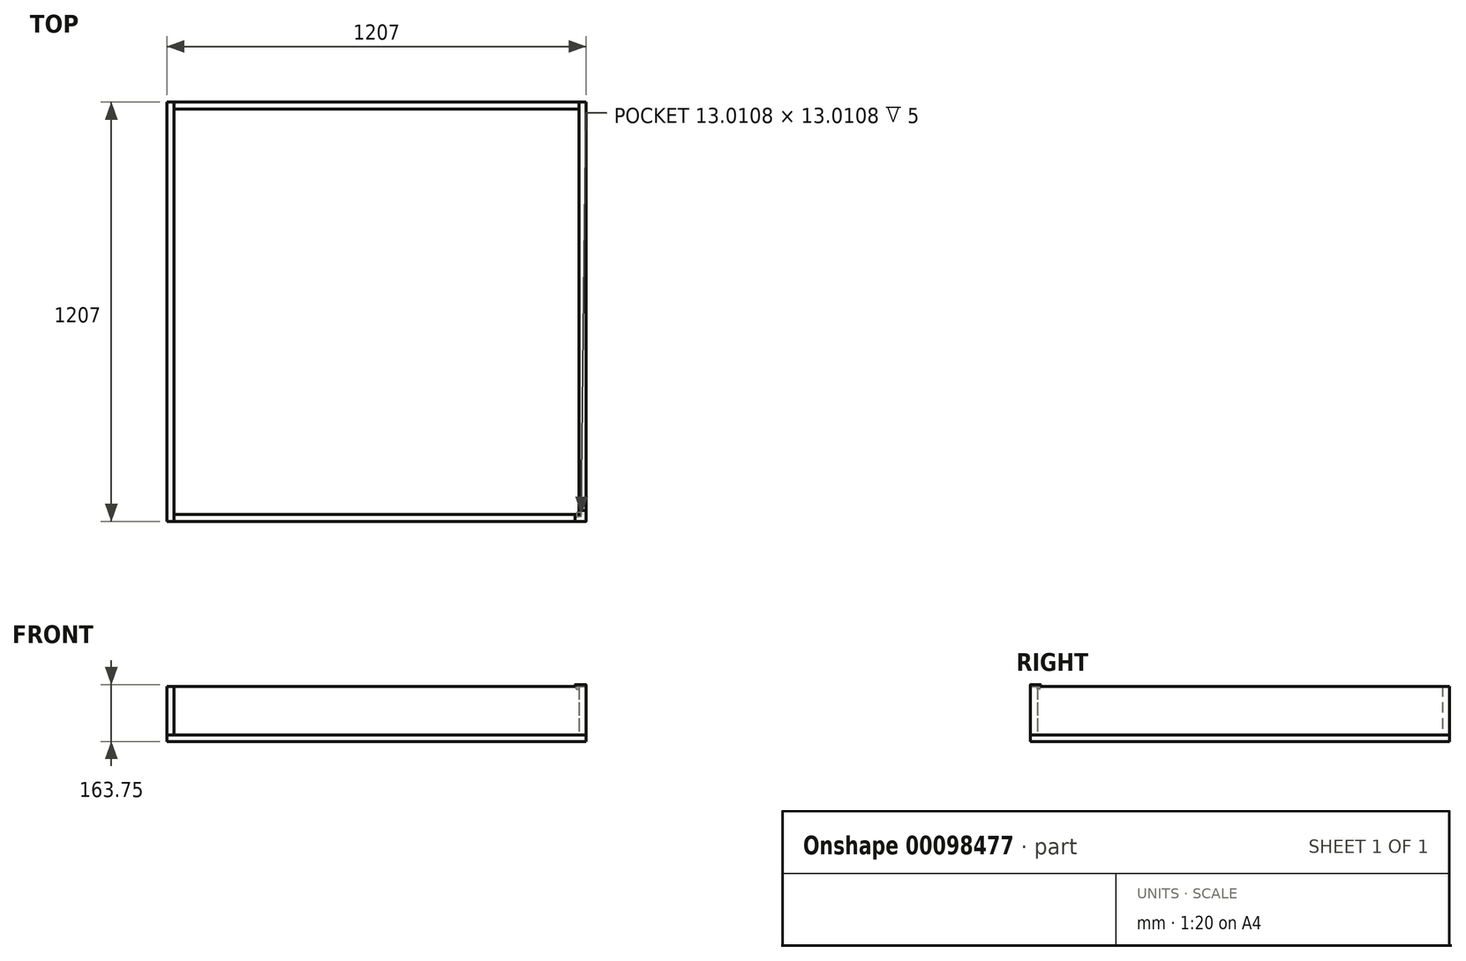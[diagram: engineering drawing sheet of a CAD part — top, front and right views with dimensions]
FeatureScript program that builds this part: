
annotation { "Feature Type Name" : "Feature", "Feature Type Description" : "" }
export const myFeature = defineFeature(function(context is Context, id is Id, definition is map)
    precondition{}
    {
        {
            var Q0;
            Q0=qCreatedBy(makeId("Top.planeOp"),FACE);
            var sketch = newSketch(context, id + "F0", { "sketchPlane" : qUnion([Q0])});
            skLineSegment(sketch, "E0.bottom", {"start": v(603.5, -603.5) * mm, "end": v(-603.5, -603.5) * mm});
            skLineSegment(sketch, "E0.top", {"start": v(603.5, 603.5) * mm, "end": v(-603.5, 603.5) * mm});
            skLineSegment(sketch, "E0.left", {"start": v(603.5, -603.5) * mm, "end": v(603.5, 603.5) * mm});
            skLineSegment(sketch, "E0.right", {"start": v(-603.5, -603.5) * mm, "end": v(-603.5, 603.5) * mm});
            skPoint(sketch, "E0.middle", {"position": v(0, 0) * mm});
            skSolve(sketch);
        }
        {
            var Q0;
            Q0 = qSketchRegion(id + "F0", true);
            extrude(context, id + "F1", {"entities" : qUnion([Q0]), "depth" : 19.05 * mm});
        }
        {
            var Q0;
            Q0=makeQuery(id+"F1.opExtrude","CAP_FACE",FACE,{"disambiguationData":[OSD([sQuery(id+"F0.wireOp",EDGE,"E0.bottom"),sQuery(id+"F0.wireOp",EDGE,"E0.top"),sQuery(id+"F0.wireOp",EDGE,"E0.left"),sQuery(id+"F0.wireOp",EDGE,"E0.right")])],"isStart":false});
            var sketch = newSketch(context, id + "F2", { "sketchPlane" : qUnion([Q0])});
            skLineSegment(sketch, "E1.0", {"start": v(-603.5, -603.5) * mm, "end": v(-603.5, 603.5) * mm});
            skLineSegment(sketch, "E1.1", {"start": v(603.5, 603.5) * mm, "end": v(-603.5, 603.5) * mm});
            skLineSegment(sketch, "E1.2", {"start": v(603.5, -603.5) * mm, "end": v(-603.5, -603.5) * mm});
            skLineSegment(sketch, "E2", {"start": v(-583.3, 603.5) * mm, "end": v(-583.3, -603.5) * mm});
            skSolve(sketch);
        }
        {
            var Q0;
            {var subQ0=sQuery(id+"F2.wireOp",EDGE,"E1.0");Q0=makeQuery(id+"F2.imprint","IMPRINT",FACE,{"disambiguationData":[TD([[makeQuery(id+"F2.imprint","IMPRINT",EDGE,{"derivedFrom":subQ0}),-1.0]])]});}
            extrude(context, id + "F3", {"entities" : qUnion([Q0]), "depth" : 139.7 * mm});
        }
        {
            var Q0;
            Q0=makeQuery(id+"F3.opExtrude","SWEPT_BODY",BODY,{"disambiguationData":[OSD([sQuery(id+"F2.wireOp",EDGE,"E1.0"),sQuery(id+"F2.wireOp",EDGE,"E1.1"),sQuery(id+"F2.wireOp",EDGE,"E1.2"),sQuery(id+"F2.wireOp",EDGE,"E2")])]});
            var Q1;
            Q1=qCreatedBy(makeId("Right.planeOp"),FACE);
            mirror(context, id + "F4", {"entities" : qUnion([Q0]), "mirrorPlane" : qUnion([Q1])});
        }
        {
            var Q0;
            Q0=makeQuery(id+"F1.opExtrude","CAP_FACE",FACE,{"disambiguationData":[OSD([sQuery(id+"F0.wireOp",EDGE,"E0.bottom"),sQuery(id+"F0.wireOp",EDGE,"E0.top"),sQuery(id+"F0.wireOp",EDGE,"E0.left"),sQuery(id+"F0.wireOp",EDGE,"E0.right")])],"isStart":false});
            var sketch = newSketch(context, id + "F5", { "sketchPlane" : qUnion([Q0])});
            skLineSegment(sketch, "E3.0", {"start": v(583.3, 603.5) * mm, "end": v(-583.3, 603.5) * mm});
            skLineSegment(sketch, "E3.1", {"start": v(-583.3, 603.5) * mm, "end": v(-583.3, -603.5) * mm});
            skLineSegment(sketch, "E3.2", {"start": v(583.3, 603.5) * mm, "end": v(583.3, -603.5) * mm});
            skLineSegment(sketch, "E4", {"start": v(-583.3, 583.3) * mm, "end": v(583.3, 583.3) * mm});
            skPoint(sketch, "E5.orphan", {"position": v(-603.5, 603.5) * mm});
            skPoint(sketch, "E6.orphan", {"position": v(603.5, 603.5) * mm});
            skSolve(sketch);
        }
        {
            var Q0;
            {var subQ0=sQuery(id+"F5.wireOp",EDGE,"E3.0");Q0=makeQuery(id+"F5.imprint","IMPRINT",FACE,{"disambiguationData":[TD([[makeQuery(id+"F5.imprint","IMPRINT",EDGE,{"derivedFrom":subQ0}),1.0]])]});}
            extrude(context, id + "F6", {"entities" : qUnion([Q0]), "depth" : 139.7 * mm});
        }
        {
            var Q0;
            Q0=makeQuery(id+"F6.opExtrude","SWEPT_BODY",BODY,{"disambiguationData":[OSD([sQuery(id+"F5.wireOp",EDGE,"E3.0"),sQuery(id+"F5.wireOp",EDGE,"E3.1"),sQuery(id+"F5.wireOp",EDGE,"E3.2"),sQuery(id+"F5.wireOp",EDGE,"E4")])]});
            var Q1;
            Q1=qCreatedBy(makeId("Front.planeOp"),FACE);
            mirror(context, id + "F7", {"entities" : qUnion([Q0]), "mirrorPlane" : qUnion([Q1])});
        }
        {
            var Q0;
            Q0=makeQuery(id+"F4.opPattern","COPY",FACE,{"derivedFrom":makeQuery(id+"F3.opExtrude","CAP_FACE",FACE,{"disambiguationData":[OSD([sQuery(id+"F2.wireOp",EDGE,"E1.0"),sQuery(id+"F2.wireOp",EDGE,"E1.1"),sQuery(id+"F2.wireOp",EDGE,"E1.2"),sQuery(id+"F2.wireOp",EDGE,"E2")])],"isStart":false}),"instanceName":"1"});
            cPlane(context, id + "F8", {"entities" : qUnion([Q0]), "cplaneType" : CPlaneType.OFFSET, "offset" : 0 * mm, "width" : 150 * mm, "height" : 150 * mm});
        }
        {
            var Q0;
            Q0=qCreatedBy(id+"F8.planeOp",FACE);
            var sketch = newSketch(context, id + "F9", { "sketchPlane" : qUnion([Q0])});
            skLineSegment(sketch, "E7.0", {"start": v(583.3, 603.5) * mm, "end": v(583.3, -603.5) * mm});
            skLineSegment(sketch, "E7.1", {"start": v(-583.3, -583.3) * mm, "end": v(583.3, -583.3) * mm});
            skLineSegment(sketch, "E7.2", {"start": v(583.3, -603.5) * mm, "end": v(603.5, -603.5) * mm});
            skLineSegment(sketch, "E7.3", {"start": v(603.5, -603.5) * mm, "end": v(603.5, 603.5) * mm});
            skLineSegment(sketch, "E7.4", {"start": v(583.3, -603.5) * mm, "end": v(-583.3, -603.5) * mm});
            skLineSegment(sketch, "E8", {"start": v(603.5, -603.5) * mm, "end": v(583.3, -583.3) * mm, "construction": true});
            skLineSegment(sketch, "E9", {"start": v(583.3, -583.3) * mm, "end": v(583.3, -583.3) * mm});
            skLineSegment(sketch, "E10", {"start": v(583.3, -583.3) * mm, "end": v(578.2, -588.4) * mm, "construction": true});
            skLineSegment(sketch, "E11.MirrorCS", {"start": v(583.3, -583.3) * mm, "end": v(588.4, -578.2) * mm, "construction": true});
            skLineSegment(sketch, "E12", {"start": v(588.4, -578.2) * mm, "end": v(586.98, -576.8) * mm});
            skLineSegment(sketch, "E13", {"start": v(586.98, -576.8) * mm, "end": v(576.8, -586.98) * mm});
            skLineSegment(sketch, "E14", {"start": v(578.2, -588.4) * mm, "end": v(576.8, -586.98) * mm});
            skLineSegment(sketch, "E15.MirrorCS", {"start": v(588.4, -578.2) * mm, "end": v(589.8, -579.62) * mm});
            skLineSegment(sketch, "E16.MirrorCS", {"start": v(589.8, -579.62) * mm, "end": v(579.62, -589.8) * mm});
            skLineSegment(sketch, "E17.MirrorCS", {"start": v(578.2, -588.4) * mm, "end": v(579.62, -589.8) * mm});
            skLineSegment(sketch, "E18.1", {"start": v(571.14, -586.98) * mm, "end": v(579.62, -595.46) * mm});
            skLineSegment(sketch, "E18.3", {"start": v(593.8, -581.28) * mm, "end": v(579.62, -595.46) * mm});
            skLineSegment(sketch, "E18.4", {"start": v(585.4, -572.71) * mm, "end": v(571.14, -586.98) * mm});
            skLineSegment(sketch, "E19.trimOffspring", {"start": v(585.4, -572.71) * mm, "end": v(593.8, -581.28) * mm});
            skSolve(sketch);
        }
        {
            var Q0;
            {var subQ1=sQuery(id+"F9.wireOp",EDGE,"E12");Q0=makeQuery(id+"F9.imprint","IMPRINT",FACE,{"disambiguationData":[TD([[makeQuery(id+"F9.imprint","IMPRINT",EDGE,{"derivedFrom":subQ1}),-1.0]])]});}
            var Q1;
            {var subQ0=sQuery(id+"F9.wireOp",EDGE,"E18.4");var subQ1=sQuery(id+"F9.wireOp",EDGE,"E7.0");var subQ2=makeQuery(id+"F9.imprint","INTERSECT",VERTEX,{"derivedFrom":[subQ1,subQ0]});Q1=makeQuery(id+"F9.imprint","IMPRINT",FACE,{"disambiguationData":[TD([[makeQuery(id+"F9.imprint","IMPRINT",EDGE,{"disambiguationData":[TD([[subQ2,-1.0]])],"derivedFrom":subQ1}),-1.0]])]});}
            var Q2;
            {var subQ0=sQuery(id+"F9.wireOp",EDGE,"E14");Q2=makeQuery(id+"F9.imprint","IMPRINT",FACE,{"disambiguationData":[TD([[makeQuery(id+"F9.imprint","IMPRINT",EDGE,{"derivedFrom":subQ0}),1.0]])]});}
            extrude(context, id + "F10", {"entities" : qUnion([Q0, Q1, Q2]), "depth" : 5 * mm});
        }
        {
            var Q0;
            Q0=makeQuery(id+"F10.opExtrude","CAP_FACE",FACE,{"disambiguationData":[OSD([sQuery(id+"F9.wireOp",EDGE,"E12"),sQuery(id+"F9.wireOp",EDGE,"E13"),sQuery(id+"F9.wireOp",EDGE,"E14"),sQuery(id+"F9.wireOp",EDGE,"E15.MirrorCS"),sQuery(id+"F9.wireOp",EDGE,"E16.MirrorCS"),sQuery(id+"F9.wireOp",EDGE,"E17.MirrorCS"),sQuery(id+"F9.wireOp",EDGE,"E18.1"),sQuery(id+"F9.wireOp",EDGE,"E18.3"),sQuery(id+"F9.wireOp",EDGE,"E18.4"),sQuery(id+"F9.wireOp",EDGE,"E19.trimOffspring")])],"isStart":true});
            var sketch = newSketch(context, id + "F11", { "sketchPlane" : qUnion([Q0])});
            skLineSegment(sketch, "E20.0", {"start": v(574.81, 583.3) * mm, "end": v(583.3, 583.3) * mm});
            skLineSegment(sketch, "E20.1", {"start": v(583.3, 574.81) * mm, "end": v(574.81, 583.3) * mm});
            skLineSegment(sketch, "E20.2", {"start": v(583.3, 574.81) * mm, "end": v(583.3, 583.3) * mm});
            skPoint(sketch, "E21.orphan", {"position": v(571.14, 586.98) * mm});
            skPoint(sketch, "E22.orphan", {"position": v(585.4, 572.71) * mm});
            skPoint(sketch, "E23.orphan", {"position": v(583.3, 603.5) * mm});
            skPoint(sketch, "E24.orphan", {"position": v(583.3, -603.5) * mm});
            skPoint(sketch, "E25.orphan", {"position": v(-583.3, 583.3) * mm});
            skSolve(sketch);
        }
        {
            var Q0;
            Q0 = qSketchRegion(id + "F11", true);
            extrude(context, id + "F12", {"entities" : qUnion([Q0]), "operationType" : NewBodyOperationType.ADD, "depth" : 8 * mm});
        }
        {
            var Q0;
            Q0=makeQuery(id+"F4.opPattern","COPY",FACE,{"derivedFrom":makeQuery(id+"F3.opExtrude","CAP_FACE",FACE,{"disambiguationData":[OSD([sQuery(id+"F2.wireOp",EDGE,"E1.0"),sQuery(id+"F2.wireOp",EDGE,"E1.1"),sQuery(id+"F2.wireOp",EDGE,"E1.2"),sQuery(id+"F2.wireOp",EDGE,"E2")])],"isStart":false}),"instanceName":"1"});
            var sketch = newSketch(context, id + "F13", { "sketchPlane" : qUnion([Q0])});
            skLineSegment(sketch, "E26.0", {"start": v(585.4, -572.71) * mm, "end": v(571.14, -586.98) * mm});
            skLineSegment(sketch, "E26.1", {"start": v(585.4, -572.71) * mm, "end": v(593.8, -581.28) * mm});
            skLineSegment(sketch, "E26.2", {"start": v(571.14, -586.98) * mm, "end": v(579.62, -595.46) * mm});
            skLineSegment(sketch, "E26.3", {"start": v(583.3, -603.5) * mm, "end": v(571.14, -603.5) * mm});
            skLineSegment(sketch, "E26.4", {"start": v(583.3, -603.5) * mm, "end": v(603.5, -603.5) * mm});
            skLineSegment(sketch, "E26.5", {"start": v(603.5, -603.5) * mm, "end": v(603.5, -572.71) * mm});
            skLineSegment(sketch, "E27", {"start": v(571.14, -586.98) * mm, "end": v(571.14, -603.5) * mm});
            skLineSegment(sketch, "E28", {"start": v(585.4, -572.71) * mm, "end": v(603.5, -572.71) * mm});
            skPoint(sketch, "E29.orphan", {"position": v(603.5, 603.5) * mm});
            skPoint(sketch, "E30.orphan", {"position": v(-583.3, -603.5) * mm});
            skLineSegment(sketch, "E31.0", {"start": v(586.98, -576.8) * mm, "end": v(576.8, -586.98) * mm});
            skLineSegment(sketch, "E31.1", {"start": v(576.8, -586.98) * mm, "end": v(579.62, -589.8) * mm});
            skLineSegment(sketch, "E31.2", {"start": v(589.8, -579.62) * mm, "end": v(579.62, -589.8) * mm});
            skLineSegment(sketch, "E31.3", {"start": v(589.8, -579.62) * mm, "end": v(586.98, -576.8) * mm});
            skSolve(sketch);
        }
        {
            var Q0;
            Q0 = qSketchRegion(id + "F13", true);
            extrude(context, id + "F14", {"entities" : qUnion([Q0]), "operationType" : NewBodyOperationType.ADD, "depth" : 5 * mm});
        }
        {
            var Q0;
            Q0=makeQuery(id+"FWGEz6HOKl7zaIQ_5.opExtrude","CAP_EDGE",EDGE,{"disambiguationData":[OSD([sQuery(id+"FWMM2qcWTSvCcv1_5.wireOp",EDGE,"91a42b95-2f72-43ae-b90d-e56b4a878e6f.2")])],"isStart":false});
            var Q1;
            Q1=makeQuery(id+"FWGEz6HOKl7zaIQ_5.opExtrude","CAP_EDGE",EDGE,{"disambiguationData":[OSD([sQuery(id+"FWMM2qcWTSvCcv1_5.wireOp",EDGE,"91a42b95-2f72-43ae-b90d-e56b4a878e6f.0"),sQuery(id+"FWMM2qcWTSvCcv1_5.wireOp",EDGE,"uNNJ07BH-av9Z-8PHK-tGRQ-SIAALudEH92Q")])],"isStart":false});
            var Q2;
            Q2=makeQuery(id+"FXsxuWA4XZEjvSx_5.opExtrude","CAP_EDGE",EDGE,{"disambiguationData":[OSD([sQuery(id+"FQtpU1Yz0KaSojl_5.wireOp",EDGE,"e276b77e-c843-4539-9ac6-c88ffc2a9d79.2"),sQuery(id+"FQtpU1Yz0KaSojl_5.wireOp",EDGE,"aJPaqFIm-4lGG-d9ap-Efmc-JLBxhRokaAjJ")])],"isStart":false});
            var Q3;
            Q3=makeQuery(id+"FXsxuWA4XZEjvSx_5.boolean.opBoolean","MERGE",EDGE,{"derivedFrom":[makeQuery(id+"F14.opExtrude","CAP_EDGE",EDGE,{"disambiguationData":[OSD([sQuery(id+"F13.wireOp",EDGE,"E28")])],"isStart":false}),makeQuery(id+"FXsxuWA4XZEjvSx_5.opExtrude","SWEPT_EDGE",EDGE,{"disambiguationData":[OSD([sQuery(id+"FQtpU1Yz0KaSojl_5.wireOp",EDGE,"e276b77e-c843-4539-9ac6-c88ffc2a9d79.0"),sQuery(id+"FQtpU1Yz0KaSojl_5.wireOp",EDGE,"e276b77e-c843-4539-9ac6-c88ffc2a9d79.2")])]})]});
            var Q4;
            Q4=makeQuery(id+"FWGEz6HOKl7zaIQ_5.boolean.opBoolean","MERGE",EDGE,{"derivedFrom":[makeQuery(id+"FXsxuWA4XZEjvSx_5.opExtrude","CAP_EDGE",EDGE,{"disambiguationData":[OSD([sQuery(id+"FQtpU1Yz0KaSojl_5.wireOp",EDGE,"e276b77e-c843-4539-9ac6-c88ffc2a9d79.0")])],"isStart":false}),makeQuery(id+"FWGEz6HOKl7zaIQ_5.opExtrude","SWEPT_EDGE",EDGE,{"disambiguationData":[OSD([sQuery(id+"FWMM2qcWTSvCcv1_5.wireOp",EDGE,"91a42b95-2f72-43ae-b90d-e56b4a878e6f.1"),sQuery(id+"FWMM2qcWTSvCcv1_5.wireOp",EDGE,"91a42b95-2f72-43ae-b90d-e56b4a878e6f.2")])]})]});
            var Q5;
            Q5=makeQuery(id+"FWGEz6HOKl7zaIQ_5.opExtrude","CAP_EDGE",EDGE,{"disambiguationData":[OSD([sQuery(id+"FWMM2qcWTSvCcv1_5.wireOp",EDGE,"91a42b95-2f72-43ae-b90d-e56b4a878e6f.1")])],"isStart":false});
            var Q6;
            Q6=makeQuery(id+"FWGEz6HOKl7zaIQ_5.boolean.opBoolean","MERGE",EDGE,{"derivedFrom":[makeQuery(id+"F14.opExtrude","CAP_EDGE",EDGE,{"disambiguationData":[OSD([sQuery(id+"F13.wireOp",EDGE,"E27")])],"isStart":false}),makeQuery(id+"FWGEz6HOKl7zaIQ_5.opExtrude","SWEPT_EDGE",EDGE,{"disambiguationData":[OSD([sQuery(id+"FWMM2qcWTSvCcv1_5.wireOp",EDGE,"91a42b95-2f72-43ae-b90d-e56b4a878e6f.0"),sQuery(id+"FWMM2qcWTSvCcv1_5.wireOp",EDGE,"91a42b95-2f72-43ae-b90d-e56b4a878e6f.1")])]})]});
            var Q7;
            Q7=makeQuery(id+"F10.opExtrude","CAP_EDGE",EDGE,{"disambiguationData":[OSD([sQuery(id+"F9.wireOp",EDGE,"E18.4")])],"isStart":false});
            fillet(context, id + "F15", {"entities" : qUnion([Q0, Q1, Q2, Q3, Q4, Q5, Q6, Q7]), "radius" : 1 * mm, "tangentPropagation" : true, "allowEdgeOverflow" : false});
        }
        {
            var Q0;
            Q0=makeQuery(id+"F14.opExtrude","CAP_EDGE",EDGE,{"disambiguationData":[OSD([sQuery(id+"F13.wireOp",EDGE,"E26.5")])],"isStart":false});
            var Q1;
            Q1=makeQuery(id+"F14.opExtrude","CAP_EDGE",EDGE,{"disambiguationData":[OSD([sQuery(id+"F13.wireOp",EDGE,"E26.3"),sQuery(id+"F13.wireOp",EDGE,"E26.4")])],"isStart":false});
            fillet(context, id + "F16", {"entities" : qUnion([Q0, Q1]), "radius" : 1 * mm, "tangentPropagation" : true, "allowEdgeOverflow" : false});
        }
    });
